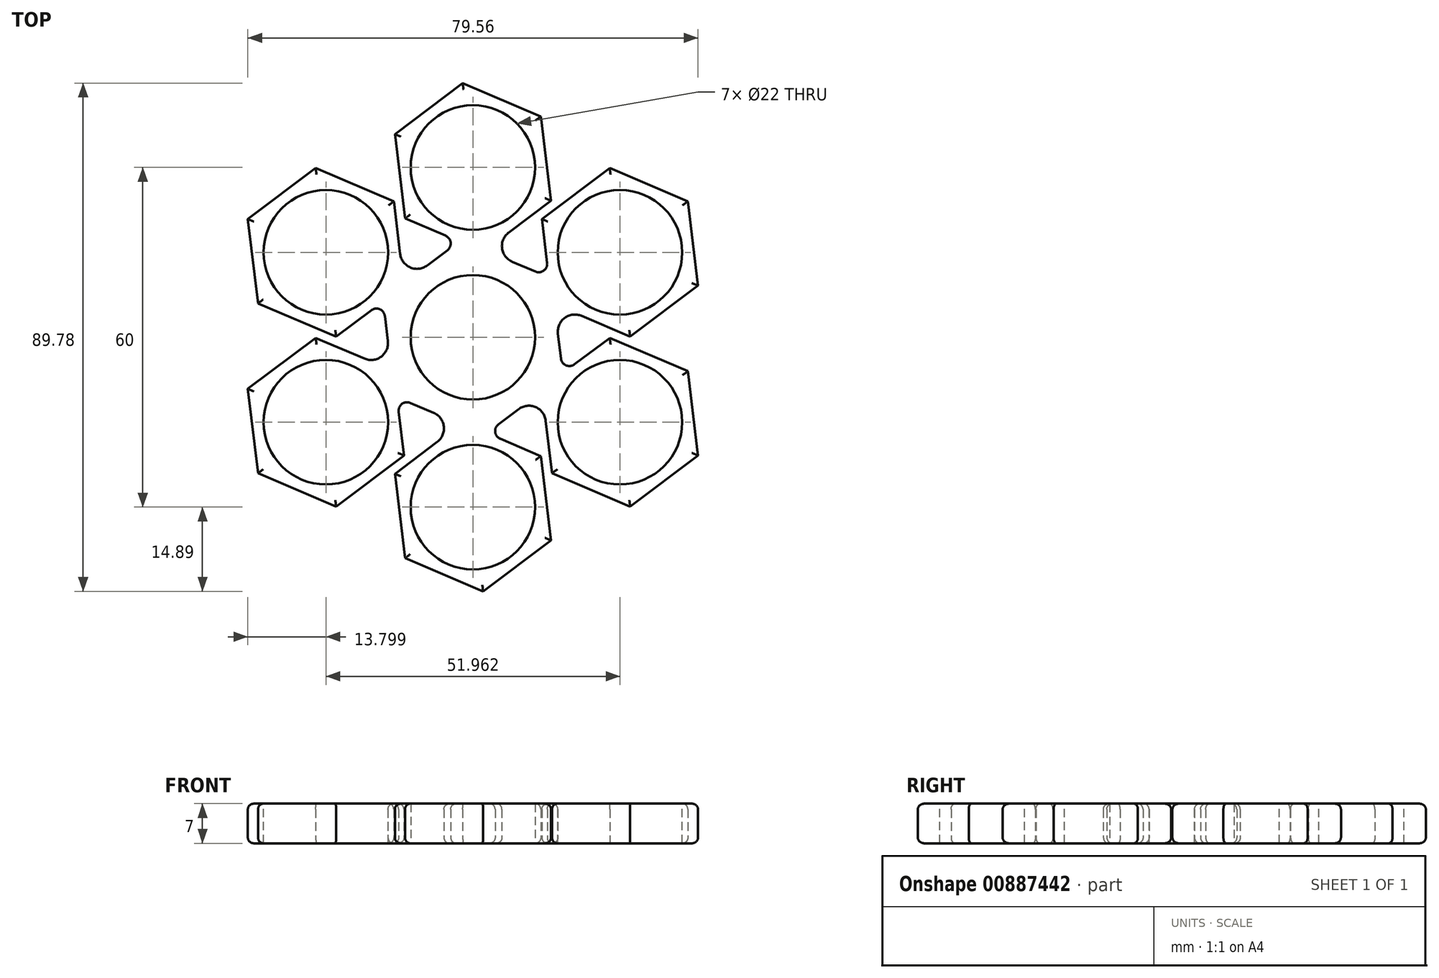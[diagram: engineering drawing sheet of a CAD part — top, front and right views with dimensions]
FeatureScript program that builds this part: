
annotation { "Feature Type Name" : "Feature", "Feature Type Description" : "" }
export const myFeature = defineFeature(function(context is Context, id is Id, definition is map)
    precondition{}
    {
        {
            var Q0;
            Q0=qCreatedBy(makeId("Top.planeOp"),FACE);
            var sketch = newSketch(context, id + "F0", { "sketchPlane" : qUnion([Q0])});
            skCircle(sketch, "E0", {"center": v(0, 0) * mm, "radius": 11 * mm});
            skCircle(sketch, "E1", {"center": v(0, 0) * mm, "radius": 15 * mm});
            skLineSegment(sketch, "E2", {"start": v(0, 0) * mm, "end": v(0, 30) * mm, "construction": true});
            skCircle(sketch, "E3", {"center": v(0, 30) * mm, "radius": 15 * mm, "construction": true});
            skLineSegment(sketch, "E4.2", {"start": v(-13.8, 35.88) * mm, "end": v(-1.8, 44.9) * mm});
            skLineSegment(sketch, "E4.3", {"start": v(-1.8, 44.9) * mm, "end": v(12, 39) * mm});
            skLineSegment(sketch, "E4.4", {"start": v(12, 39) * mm, "end": v(13.8, 24.12) * mm});
            skLineSegment(sketch, "E4.5", {"start": v(13.8, 24.12) * mm, "end": v(1.55, 14.92) * mm});
            skLineSegment(sketch, "E5.0", {"start": v(9.55, 25.93) * mm, "end": v(-9, 12) * mm});
            skLineSegment(sketch, "E5.1", {"start": v(8.3, 36.23) * mm, "end": v(9.55, 25.93) * mm});
            skLineSegment(sketch, "E5.2", {"start": v(-1.25, 40.3) * mm, "end": v(8.3, 36.23) * mm});
            skLineSegment(sketch, "E5.3", {"start": v(-11.4, 32.69) * mm, "end": v(-1.25, 40.3) * mm});
            skLineSegment(sketch, "E6", {"start": v(-11.4, 32.69) * mm, "end": v(-13.8, 35.88) * mm, "construction": true});
            skLineSegment(sketch, "E7", {"start": v(-12.6, 34.29) * mm, "end": v(-13.52, 33.6) * mm, "construction": true});
            skLineSegment(sketch, "E8", {"start": v(-13.52, 33.6) * mm, "end": v(-13.8, 35.88) * mm});
            skLineSegment(sketch, "E9", {"start": v(-11.4, 32.69) * mm, "end": v(-13.52, 33.6) * mm});
            skLineSegment(sketch, "E10.1.0", {"start": v(-37.98, 6) * mm, "end": v(-39.78, 20.88) * mm});
            skLineSegment(sketch, "E10.1.1", {"start": v(-39.78, 20.88) * mm, "end": v(-27.78, 29.9) * mm});
            skLineSegment(sketch, "E10.1.2", {"start": v(-34, 6.47) * mm, "end": v(-35.53, 19.07) * mm});
            skLineSegment(sketch, "E10.1.3", {"start": v(-35.53, 19.07) * mm, "end": v(-27.23, 25.3) * mm});
            skLineSegment(sketch, "E10.1.4", {"start": v(-35.85, 5.09) * mm, "end": v(-37.98, 6) * mm});
            skLineSegment(sketch, "E10.1.5", {"start": v(-34, 6.47) * mm, "end": v(-35.85, 5.09) * mm});
            skLineSegment(sketch, "E10.1.6", {"start": v(-27.78, 29.9) * mm, "end": v(-13.99, 24) * mm});
            skLineSegment(sketch, "E10.1.7", {"start": v(-27.23, 25.3) * mm, "end": v(-17.68, 21.23) * mm});
            skLineSegment(sketch, "E10.1.8", {"start": v(-13.99, 24) * mm, "end": v(-12.15, 8.8) * mm});
            skLineSegment(sketch, "E10.1.9", {"start": v(-17.68, 21.23) * mm, "end": v(-14.9, -1.8) * mm});
            skLineSegment(sketch, "E10.2.0", {"start": v(-24.18, -29.9) * mm, "end": v(-37.98, -24) * mm});
            skLineSegment(sketch, "E10.2.1", {"start": v(-37.98, -24) * mm, "end": v(-39.78, -9.12) * mm});
            skLineSegment(sketch, "E10.2.2", {"start": v(-22.6, -26.21) * mm, "end": v(-34.28, -21.23) * mm});
            skLineSegment(sketch, "E10.2.3", {"start": v(-34.28, -21.23) * mm, "end": v(-35.53, -10.93) * mm});
            skLineSegment(sketch, "E10.2.4", {"start": v(-22.33, -28.5) * mm, "end": v(-24.18, -29.9) * mm});
            skLineSegment(sketch, "E10.2.5", {"start": v(-22.6, -26.21) * mm, "end": v(-22.33, -28.5) * mm});
            skLineSegment(sketch, "E10.2.6", {"start": v(-39.78, -9.12) * mm, "end": v(-27.78, -0.1) * mm});
            skLineSegment(sketch, "E10.2.7", {"start": v(-35.53, -10.93) * mm, "end": v(-27.23, -4.7) * mm});
            skLineSegment(sketch, "E10.2.8", {"start": v(-27.78, -0.1) * mm, "end": v(-13.7, -6.12) * mm});
            skLineSegment(sketch, "E10.2.9", {"start": v(-27.23, -4.7) * mm, "end": v(-5.88, -13.8) * mm});
            skLineSegment(sketch, "E10.3.0", {"start": v(13.8, -35.88) * mm, "end": v(1.8, -44.9) * mm});
            skLineSegment(sketch, "E10.3.1", {"start": v(1.8, -44.9) * mm, "end": v(-12, -39) * mm});
            skLineSegment(sketch, "E10.3.2", {"start": v(11.4, -32.69) * mm, "end": v(1.25, -40.3) * mm});
            skLineSegment(sketch, "E10.3.3", {"start": v(1.25, -40.3) * mm, "end": v(-8.3, -36.23) * mm});
            skLineSegment(sketch, "E10.3.4", {"start": v(13.52, -33.6) * mm, "end": v(13.8, -35.88) * mm});
            skLineSegment(sketch, "E10.3.5", {"start": v(11.4, -32.69) * mm, "end": v(13.52, -33.6) * mm});
            skLineSegment(sketch, "E10.3.6", {"start": v(-12, -39) * mm, "end": v(-13.8, -24.12) * mm});
            skLineSegment(sketch, "E10.3.7", {"start": v(-8.3, -36.23) * mm, "end": v(-9.55, -25.93) * mm});
            skLineSegment(sketch, "E10.3.8", {"start": v(-13.8, -24.12) * mm, "end": v(-1.55, -14.92) * mm});
            skLineSegment(sketch, "E10.3.9", {"start": v(-9.55, -25.93) * mm, "end": v(9, -12) * mm});
            skLineSegment(sketch, "E10.4.0", {"start": v(37.98, -6) * mm, "end": v(39.78, -20.88) * mm});
            skLineSegment(sketch, "E10.4.1", {"start": v(39.78, -20.88) * mm, "end": v(27.78, -29.9) * mm});
            skLineSegment(sketch, "E10.4.2", {"start": v(34, -6.47) * mm, "end": v(35.53, -19.07) * mm});
            skLineSegment(sketch, "E10.4.3", {"start": v(35.53, -19.07) * mm, "end": v(27.23, -25.3) * mm});
            skLineSegment(sketch, "E10.4.4", {"start": v(35.85, -5.09) * mm, "end": v(37.98, -6) * mm});
            skLineSegment(sketch, "E10.4.5", {"start": v(34, -6.47) * mm, "end": v(35.85, -5.09) * mm});
            skLineSegment(sketch, "E10.4.6", {"start": v(27.78, -29.9) * mm, "end": v(13.99, -24) * mm});
            skLineSegment(sketch, "E10.4.7", {"start": v(27.23, -25.3) * mm, "end": v(17.68, -21.23) * mm});
            skLineSegment(sketch, "E10.4.8", {"start": v(13.99, -24) * mm, "end": v(12.15, -8.8) * mm});
            skLineSegment(sketch, "E10.4.9", {"start": v(17.68, -21.23) * mm, "end": v(14.9, 1.8) * mm});
            skLineSegment(sketch, "E10.5.0", {"start": v(24.18, 29.9) * mm, "end": v(37.98, 24) * mm});
            skLineSegment(sketch, "E10.5.1", {"start": v(37.98, 24) * mm, "end": v(39.78, 9.12) * mm});
            skLineSegment(sketch, "E10.5.2", {"start": v(22.6, 26.21) * mm, "end": v(34.28, 21.23) * mm});
            skLineSegment(sketch, "E10.5.3", {"start": v(34.28, 21.23) * mm, "end": v(35.53, 10.93) * mm});
            skLineSegment(sketch, "E10.5.4", {"start": v(22.33, 28.5) * mm, "end": v(24.18, 29.9) * mm});
            skLineSegment(sketch, "E10.5.5", {"start": v(22.6, 26.21) * mm, "end": v(22.33, 28.5) * mm});
            skLineSegment(sketch, "E10.5.6", {"start": v(39.78, 9.12) * mm, "end": v(27.78, 0.1) * mm});
            skLineSegment(sketch, "E10.5.7", {"start": v(35.53, 10.93) * mm, "end": v(27.23, 4.7) * mm});
            skLineSegment(sketch, "E10.5.8", {"start": v(27.78, 0.1) * mm, "end": v(13.7, 6.12) * mm});
            skLineSegment(sketch, "E10.5.9", {"start": v(27.23, 4.7) * mm, "end": v(5.88, 13.8) * mm});
            skLineSegment(sketch, "E11.1", {"start": v(13.8, 24.12) * mm, "end": v(1.8, 15.1) * mm});
            skLineSegment(sketch, "E11.2", {"start": v(1.8, 15.1) * mm, "end": v(-12, 21) * mm});
            skLineSegment(sketch, "E11.3", {"start": v(-12, 21) * mm, "end": v(-13.8, 35.88) * mm});
            skLineSegment(sketch, "E12.1.0", {"start": v(-24.18, 0.1) * mm, "end": v(-37.98, 6) * mm});
            skLineSegment(sketch, "E12.1.1", {"start": v(-12.18, 9.12) * mm, "end": v(-24.18, 0.1) * mm});
            skLineSegment(sketch, "E12.2.0", {"start": v(-12.18, -20.88) * mm, "end": v(-24.18, -29.9) * mm});
            skLineSegment(sketch, "E12.2.1", {"start": v(-13.99, -6) * mm, "end": v(-12.18, -20.88) * mm});
            skLineSegment(sketch, "E12.3.0", {"start": v(12, -21) * mm, "end": v(13.8, -35.88) * mm});
            skLineSegment(sketch, "E12.3.1", {"start": v(-1.8, -15.1) * mm, "end": v(12, -21) * mm});
            skLineSegment(sketch, "E12.4.0", {"start": v(24.18, -0.1) * mm, "end": v(37.98, -6) * mm});
            skLineSegment(sketch, "E12.4.1", {"start": v(12.18, -9.12) * mm, "end": v(24.18, -0.1) * mm});
            skLineSegment(sketch, "E12.5.0", {"start": v(12.18, 20.88) * mm, "end": v(24.18, 29.9) * mm});
            skLineSegment(sketch, "E12.5.1", {"start": v(13.99, 6) * mm, "end": v(12.18, 20.88) * mm});
            skSolve(sketch);
        }
        {
            var Q0;
            Q0 = qSketchRegion(id + "F0", true);
            extrude(context, id + "F1", {"entities" : qUnion([Q0]), "depth" : 7 * mm, "offsetDistance" : 25 * mm});
        }
        {
            var Q0;
            Q0=makeQuery(id+"F1.opExtrude","SWEPT_EDGE",EDGE,{"disambiguationData":[OSD([sQuery(id+"F0.wireOp",EDGE,"E5.0"),sQuery(id+"F0.wireOp",EDGE,"E11.2")])]});
            var Q1;
            Q1=makeQuery(id+"F1.opExtrude","SWEPT_EDGE",EDGE,{"disambiguationData":[OSD([sQuery(id+"F0.wireOp",EDGE,"E10.5.9"),sQuery(id+"F0.wireOp",EDGE,"E12.5.1")])]});
            var Q2;
            Q2=makeQuery(id+"F1.opExtrude","SWEPT_EDGE",EDGE,{"disambiguationData":[OSD([sQuery(id+"F0.wireOp",EDGE,"E10.4.9"),sQuery(id+"F0.wireOp",EDGE,"E12.4.1")])]});
            var Q3;
            Q3=makeQuery(id+"F1.opExtrude","SWEPT_EDGE",EDGE,{"disambiguationData":[OSD([sQuery(id+"F0.wireOp",EDGE,"E10.3.9"),sQuery(id+"F0.wireOp",EDGE,"E12.3.1")])]});
            var Q4;
            Q4=makeQuery(id+"F1.opExtrude","SWEPT_EDGE",EDGE,{"disambiguationData":[OSD([sQuery(id+"F0.wireOp",EDGE,"E10.2.9"),sQuery(id+"F0.wireOp",EDGE,"E12.2.1")])]});
            var Q5;
            Q5=makeQuery(id+"F1.opExtrude","SWEPT_EDGE",EDGE,{"disambiguationData":[OSD([sQuery(id+"F0.wireOp",EDGE,"E10.1.9"),sQuery(id+"F0.wireOp",EDGE,"E12.1.1")])]});
            fillet(context, id + "F2", {"entities" : qUnion([Q0, Q1, Q2, Q3, Q4, Q5]), "radius" : 1.5 * mm, "tangentPropagation" : true, "allowEdgeOverflow" : false});
        }
        {
            var Q0;
            Q0=makeQuery(id+"F1.opExtrude","SWEPT_EDGE",EDGE,{"disambiguationData":[OSD([sQuery(id+"F0.wireOp",EDGE,"E1"),sQuery(id+"F0.wireOp",EDGE,"E10.3.8")])]});
            var Q1;
            Q1=makeQuery(id+"F1.opExtrude","SWEPT_EDGE",EDGE,{"disambiguationData":[OSD([sQuery(id+"F0.wireOp",EDGE,"E1"),sQuery(id+"F0.wireOp",EDGE,"E10.2.8")])]});
            var Q2;
            Q2=makeQuery(id+"F1.opExtrude","SWEPT_EDGE",EDGE,{"disambiguationData":[OSD([sQuery(id+"F0.wireOp",EDGE,"E1"),sQuery(id+"F0.wireOp",EDGE,"E10.1.8")])]});
            var Q3;
            Q3=makeQuery(id+"F1.opExtrude","SWEPT_EDGE",EDGE,{"disambiguationData":[OSD([sQuery(id+"F0.wireOp",EDGE,"E1"),sQuery(id+"F0.wireOp",EDGE,"E4.5")])]});
            var Q4;
            Q4=makeQuery(id+"F1.opExtrude","SWEPT_EDGE",EDGE,{"disambiguationData":[OSD([sQuery(id+"F0.wireOp",EDGE,"E1"),sQuery(id+"F0.wireOp",EDGE,"E10.5.8")])]});
            var Q5;
            Q5=makeQuery(id+"F1.opExtrude","SWEPT_EDGE",EDGE,{"disambiguationData":[OSD([sQuery(id+"F0.wireOp",EDGE,"E1"),sQuery(id+"F0.wireOp",EDGE,"E10.4.8")])]});
            fillet(context, id + "F3", {"entities" : qUnion([Q0, Q1, Q2, Q3, Q4, Q5]), "radius" : 3 * mm, "tangentPropagation" : true, "allowEdgeOverflow" : false});
        }
        {
            var Q0;
            Q0=makeQuery(id+"F1.opExtrude","CAP_FACE",FACE,{"disambiguationData":[OSD([sQuery(id+"F0.wireOp",EDGE,"E0"),sQuery(id+"F0.wireOp",EDGE,"E1"),sQuery(id+"F0.wireOp",EDGE,"E4.2"),sQuery(id+"F0.wireOp",EDGE,"E4.3"),sQuery(id+"F0.wireOp",EDGE,"E4.4"),sQuery(id+"F0.wireOp",EDGE,"E4.5"),sQuery(id+"F0.wireOp",EDGE,"E5.0"),sQuery(id+"F0.wireOp",EDGE,"E5.1"),sQuery(id+"F0.wireOp",EDGE,"E5.2"),sQuery(id+"F0.wireOp",EDGE,"E5.3"),sQuery(id+"F0.wireOp",EDGE,"E8"),sQuery(id+"F0.wireOp",EDGE,"E9"),sQuery(id+"F0.wireOp",EDGE,"E10.1.0"),sQuery(id+"F0.wireOp",EDGE,"E10.1.1"),sQuery(id+"F0.wireOp",EDGE,"E10.1.2"),sQuery(id+"F0.wireOp",EDGE,"E10.1.3"),sQuery(id+"F0.wireOp",EDGE,"E10.1.4"),sQuery(id+"F0.wireOp",EDGE,"E10.1.5"),sQuery(id+"F0.wireOp",EDGE,"E10.1.6"),sQuery(id+"F0.wireOp",EDGE,"E10.1.7"),sQuery(id+"F0.wireOp",EDGE,"E10.1.8"),sQuery(id+"F0.wireOp",EDGE,"E10.1.9"),sQuery(id+"F0.wireOp",EDGE,"E10.2.0"),sQuery(id+"F0.wireOp",EDGE,"E10.2.1"),sQuery(id+"F0.wireOp",EDGE,"E10.2.2"),sQuery(id+"F0.wireOp",EDGE,"E10.2.3"),sQuery(id+"F0.wireOp",EDGE,"E10.2.4"),sQuery(id+"F0.wireOp",EDGE,"E10.2.5"),sQuery(id+"F0.wireOp",EDGE,"E10.2.6"),sQuery(id+"F0.wireOp",EDGE,"E10.2.7"),sQuery(id+"F0.wireOp",EDGE,"E10.2.8"),sQuery(id+"F0.wireOp",EDGE,"E10.2.9"),sQuery(id+"F0.wireOp",EDGE,"E10.3.0"),sQuery(id+"F0.wireOp",EDGE,"E10.3.1"),sQuery(id+"F0.wireOp",EDGE,"E10.3.2"),sQuery(id+"F0.wireOp",EDGE,"E10.3.3"),sQuery(id+"F0.wireOp",EDGE,"E10.3.4"),sQuery(id+"F0.wireOp",EDGE,"E10.3.5"),sQuery(id+"F0.wireOp",EDGE,"E10.3.6"),sQuery(id+"F0.wireOp",EDGE,"E10.3.7"),sQuery(id+"F0.wireOp",EDGE,"E10.3.8"),sQuery(id+"F0.wireOp",EDGE,"E10.3.9"),sQuery(id+"F0.wireOp",EDGE,"E10.4.0"),sQuery(id+"F0.wireOp",EDGE,"E10.4.1"),sQuery(id+"F0.wireOp",EDGE,"E10.4.2"),sQuery(id+"F0.wireOp",EDGE,"E10.4.3"),sQuery(id+"F0.wireOp",EDGE,"E10.4.4"),sQuery(id+"F0.wireOp",EDGE,"E10.4.5"),sQuery(id+"F0.wireOp",EDGE,"E10.4.6"),sQuery(id+"F0.wireOp",EDGE,"E10.4.7"),sQuery(id+"F0.wireOp",EDGE,"E10.4.8"),sQuery(id+"F0.wireOp",EDGE,"E10.4.9"),sQuery(id+"F0.wireOp",EDGE,"E10.5.0"),sQuery(id+"F0.wireOp",EDGE,"E10.5.1"),sQuery(id+"F0.wireOp",EDGE,"E10.5.2"),sQuery(id+"F0.wireOp",EDGE,"E10.5.3"),sQuery(id+"F0.wireOp",EDGE,"E10.5.4"),sQuery(id+"F0.wireOp",EDGE,"E10.5.5"),sQuery(id+"F0.wireOp",EDGE,"E10.5.6"),sQuery(id+"F0.wireOp",EDGE,"E10.5.7"),sQuery(id+"F0.wireOp",EDGE,"E10.5.8"),sQuery(id+"F0.wireOp",EDGE,"E10.5.9")])],"isStart":true});
            var Q1;
            Q1=makeQuery(id+"F1.opExtrude","CAP_FACE",FACE,{"disambiguationData":[OSD([sQuery(id+"F0.wireOp",EDGE,"E0"),sQuery(id+"F0.wireOp",EDGE,"E1"),sQuery(id+"F0.wireOp",EDGE,"E4.2"),sQuery(id+"F0.wireOp",EDGE,"E4.3"),sQuery(id+"F0.wireOp",EDGE,"E4.4"),sQuery(id+"F0.wireOp",EDGE,"E4.5"),sQuery(id+"F0.wireOp",EDGE,"E5.0"),sQuery(id+"F0.wireOp",EDGE,"E5.1"),sQuery(id+"F0.wireOp",EDGE,"E5.2"),sQuery(id+"F0.wireOp",EDGE,"E5.3"),sQuery(id+"F0.wireOp",EDGE,"E8"),sQuery(id+"F0.wireOp",EDGE,"E9"),sQuery(id+"F0.wireOp",EDGE,"E10.1.0"),sQuery(id+"F0.wireOp",EDGE,"E10.1.1"),sQuery(id+"F0.wireOp",EDGE,"E10.1.2"),sQuery(id+"F0.wireOp",EDGE,"E10.1.3"),sQuery(id+"F0.wireOp",EDGE,"E10.1.4"),sQuery(id+"F0.wireOp",EDGE,"E10.1.5"),sQuery(id+"F0.wireOp",EDGE,"E10.1.6"),sQuery(id+"F0.wireOp",EDGE,"E10.1.7"),sQuery(id+"F0.wireOp",EDGE,"E10.1.8"),sQuery(id+"F0.wireOp",EDGE,"E10.1.9"),sQuery(id+"F0.wireOp",EDGE,"E10.2.0"),sQuery(id+"F0.wireOp",EDGE,"E10.2.1"),sQuery(id+"F0.wireOp",EDGE,"E10.2.2"),sQuery(id+"F0.wireOp",EDGE,"E10.2.3"),sQuery(id+"F0.wireOp",EDGE,"E10.2.4"),sQuery(id+"F0.wireOp",EDGE,"E10.2.5"),sQuery(id+"F0.wireOp",EDGE,"E10.2.6"),sQuery(id+"F0.wireOp",EDGE,"E10.2.7"),sQuery(id+"F0.wireOp",EDGE,"E10.2.8"),sQuery(id+"F0.wireOp",EDGE,"E10.2.9"),sQuery(id+"F0.wireOp",EDGE,"E10.3.0"),sQuery(id+"F0.wireOp",EDGE,"E10.3.1"),sQuery(id+"F0.wireOp",EDGE,"E10.3.2"),sQuery(id+"F0.wireOp",EDGE,"E10.3.3"),sQuery(id+"F0.wireOp",EDGE,"E10.3.4"),sQuery(id+"F0.wireOp",EDGE,"E10.3.5"),sQuery(id+"F0.wireOp",EDGE,"E10.3.6"),sQuery(id+"F0.wireOp",EDGE,"E10.3.7"),sQuery(id+"F0.wireOp",EDGE,"E10.3.8"),sQuery(id+"F0.wireOp",EDGE,"E10.3.9"),sQuery(id+"F0.wireOp",EDGE,"E10.4.0"),sQuery(id+"F0.wireOp",EDGE,"E10.4.1"),sQuery(id+"F0.wireOp",EDGE,"E10.4.2"),sQuery(id+"F0.wireOp",EDGE,"E10.4.3"),sQuery(id+"F0.wireOp",EDGE,"E10.4.4"),sQuery(id+"F0.wireOp",EDGE,"E10.4.5"),sQuery(id+"F0.wireOp",EDGE,"E10.4.6"),sQuery(id+"F0.wireOp",EDGE,"E10.4.7"),sQuery(id+"F0.wireOp",EDGE,"E10.4.8"),sQuery(id+"F0.wireOp",EDGE,"E10.4.9"),sQuery(id+"F0.wireOp",EDGE,"E10.5.0"),sQuery(id+"F0.wireOp",EDGE,"E10.5.1"),sQuery(id+"F0.wireOp",EDGE,"E10.5.2"),sQuery(id+"F0.wireOp",EDGE,"E10.5.3"),sQuery(id+"F0.wireOp",EDGE,"E10.5.4"),sQuery(id+"F0.wireOp",EDGE,"E10.5.5"),sQuery(id+"F0.wireOp",EDGE,"E10.5.6"),sQuery(id+"F0.wireOp",EDGE,"E10.5.7"),sQuery(id+"F0.wireOp",EDGE,"E10.5.8"),sQuery(id+"F0.wireOp",EDGE,"E10.5.9")])],"isStart":false});
            fillet(context, id + "F4", {"entities" : qUnion([Q0, Q1]), "radius" : 1 * mm, "tangentPropagation" : true, "allowEdgeOverflow" : false});
        }
        {
            var Q0;
            Q0=qCreatedBy(makeId("Top.planeOp"),FACE);
            var sketch = newSketch(context, id + "F5", { "sketchPlane" : qUnion([Q0])});
            skCircle(sketch, "E13", {"center": v(0, 0) * mm, "radius": 11 * mm});
            skCircle(sketch, "E14", {"center": v(0, 0) * mm, "radius": 13.02 * mm});
            skSolve(sketch);
        }
        {
            var Q0;
            Q0=makeQuery(id+"F5.imprint","IMPRINT",FACE,{"disambiguationData":[TD([[makeQuery(id+"F5.imprint","IMPRINT",EDGE,{"derivedFrom":sQuery(id+"F5.wireOp",EDGE,"E13")}),-1.0]])]});
            var Q1;
            Q1=makeQuery(id+"F1.opExtrude","CAP_FACE",FACE,{"disambiguationData":[OSD([sQuery(id+"F0.wireOp",EDGE,"E0"),sQuery(id+"F0.wireOp",EDGE,"E1"),sQuery(id+"F0.wireOp",EDGE,"E4.2"),sQuery(id+"F0.wireOp",EDGE,"E4.3"),sQuery(id+"F0.wireOp",EDGE,"E4.4"),sQuery(id+"F0.wireOp",EDGE,"E4.5"),sQuery(id+"F0.wireOp",EDGE,"E5.0"),sQuery(id+"F0.wireOp",EDGE,"E5.1"),sQuery(id+"F0.wireOp",EDGE,"E5.2"),sQuery(id+"F0.wireOp",EDGE,"E5.3"),sQuery(id+"F0.wireOp",EDGE,"E8"),sQuery(id+"F0.wireOp",EDGE,"E9"),sQuery(id+"F0.wireOp",EDGE,"E10.1.0"),sQuery(id+"F0.wireOp",EDGE,"E10.1.1"),sQuery(id+"F0.wireOp",EDGE,"E10.1.2"),sQuery(id+"F0.wireOp",EDGE,"E10.1.3"),sQuery(id+"F0.wireOp",EDGE,"E10.1.4"),sQuery(id+"F0.wireOp",EDGE,"E10.1.5"),sQuery(id+"F0.wireOp",EDGE,"E10.1.6"),sQuery(id+"F0.wireOp",EDGE,"E10.1.7"),sQuery(id+"F0.wireOp",EDGE,"E10.1.8"),sQuery(id+"F0.wireOp",EDGE,"E10.1.9"),sQuery(id+"F0.wireOp",EDGE,"E10.2.0"),sQuery(id+"F0.wireOp",EDGE,"E10.2.1"),sQuery(id+"F0.wireOp",EDGE,"E10.2.2"),sQuery(id+"F0.wireOp",EDGE,"E10.2.3"),sQuery(id+"F0.wireOp",EDGE,"E10.2.4"),sQuery(id+"F0.wireOp",EDGE,"E10.2.5"),sQuery(id+"F0.wireOp",EDGE,"E10.2.6"),sQuery(id+"F0.wireOp",EDGE,"E10.2.7"),sQuery(id+"F0.wireOp",EDGE,"E10.2.8"),sQuery(id+"F0.wireOp",EDGE,"E10.2.9"),sQuery(id+"F0.wireOp",EDGE,"E10.3.0"),sQuery(id+"F0.wireOp",EDGE,"E10.3.1"),sQuery(id+"F0.wireOp",EDGE,"E10.3.2"),sQuery(id+"F0.wireOp",EDGE,"E10.3.3"),sQuery(id+"F0.wireOp",EDGE,"E10.3.4"),sQuery(id+"F0.wireOp",EDGE,"E10.3.5"),sQuery(id+"F0.wireOp",EDGE,"E10.3.6"),sQuery(id+"F0.wireOp",EDGE,"E10.3.7"),sQuery(id+"F0.wireOp",EDGE,"E10.3.8"),sQuery(id+"F0.wireOp",EDGE,"E10.3.9"),sQuery(id+"F0.wireOp",EDGE,"E10.4.0"),sQuery(id+"F0.wireOp",EDGE,"E10.4.1"),sQuery(id+"F0.wireOp",EDGE,"E10.4.2"),sQuery(id+"F0.wireOp",EDGE,"E10.4.3"),sQuery(id+"F0.wireOp",EDGE,"E10.4.4"),sQuery(id+"F0.wireOp",EDGE,"E10.4.5"),sQuery(id+"F0.wireOp",EDGE,"E10.4.6"),sQuery(id+"F0.wireOp",EDGE,"E10.4.7"),sQuery(id+"F0.wireOp",EDGE,"E10.4.8"),sQuery(id+"F0.wireOp",EDGE,"E10.4.9"),sQuery(id+"F0.wireOp",EDGE,"E10.5.0"),sQuery(id+"F0.wireOp",EDGE,"E10.5.1"),sQuery(id+"F0.wireOp",EDGE,"E10.5.2"),sQuery(id+"F0.wireOp",EDGE,"E10.5.3"),sQuery(id+"F0.wireOp",EDGE,"E10.5.4"),sQuery(id+"F0.wireOp",EDGE,"E10.5.5"),sQuery(id+"F0.wireOp",EDGE,"E10.5.6"),sQuery(id+"F0.wireOp",EDGE,"E10.5.7"),sQuery(id+"F0.wireOp",EDGE,"E10.5.8"),sQuery(id+"F0.wireOp",EDGE,"E10.5.9")])],"isStart":false});
            extrude(context, id + "F6", {"entities" : qUnion([Q0]), "operationType" : NewBodyOperationType.ADD, "endBound" : BoundingType.UP_TO_SURFACE, "depth" : 25 * mm, "endBoundEntityFace" : qUnion([Q1]), "offsetDistance" : 25 * mm});
        }
        {
            var Q0;
            Q0=makeQuery(id+"F6.boolean.opBoolean","MERGE",FACE,{"derivedFrom":[makeQuery(id+"F1.opExtrude","CAP_FACE",FACE,{"disambiguationData":[OSD([sQuery(id+"F0.wireOp",EDGE,"E0"),sQuery(id+"F0.wireOp",EDGE,"E1"),sQuery(id+"F0.wireOp",EDGE,"E4.5"),sQuery(id+"F0.wireOp",EDGE,"E5.0"),sQuery(id+"F0.wireOp",EDGE,"E10.1.0"),sQuery(id+"F0.wireOp",EDGE,"E10.1.1"),sQuery(id+"F0.wireOp",EDGE,"E10.1.6"),sQuery(id+"F0.wireOp",EDGE,"E10.1.8"),sQuery(id+"F0.wireOp",EDGE,"E10.1.9"),sQuery(id+"F0.wireOp",EDGE,"E10.2.0"),sQuery(id+"F0.wireOp",EDGE,"E10.2.1"),sQuery(id+"F0.wireOp",EDGE,"E10.2.6"),sQuery(id+"F0.wireOp",EDGE,"E10.2.8"),sQuery(id+"F0.wireOp",EDGE,"E10.2.9"),sQuery(id+"F0.wireOp",EDGE,"E10.3.0"),sQuery(id+"F0.wireOp",EDGE,"E10.3.1"),sQuery(id+"F0.wireOp",EDGE,"E10.3.6"),sQuery(id+"F0.wireOp",EDGE,"E10.3.8"),sQuery(id+"F0.wireOp",EDGE,"E10.3.9"),sQuery(id+"F0.wireOp",EDGE,"E10.4.0"),sQuery(id+"F0.wireOp",EDGE,"E10.4.1"),sQuery(id+"F0.wireOp",EDGE,"E10.4.6"),sQuery(id+"F0.wireOp",EDGE,"E10.4.8"),sQuery(id+"F0.wireOp",EDGE,"E10.4.9"),sQuery(id+"F0.wireOp",EDGE,"E10.5.0"),sQuery(id+"F0.wireOp",EDGE,"E10.5.1"),sQuery(id+"F0.wireOp",EDGE,"E10.5.6"),sQuery(id+"F0.wireOp",EDGE,"E10.5.8"),sQuery(id+"F0.wireOp",EDGE,"E10.5.9"),sQuery(id+"F0.wireOp",EDGE,"E4.4"),sQuery(id+"F0.wireOp",EDGE,"E11.1"),sQuery(id+"F0.wireOp",EDGE,"E11.2"),sQuery(id+"F0.wireOp",EDGE,"E11.3"),sQuery(id+"F0.wireOp",EDGE,"E4.2"),sQuery(id+"F0.wireOp",EDGE,"E4.3"),sQuery(id+"F0.wireOp",EDGE,"E12.1.0"),sQuery(id+"F0.wireOp",EDGE,"E12.1.1"),sQuery(id+"F0.wireOp",EDGE,"E12.2.0"),sQuery(id+"F0.wireOp",EDGE,"E12.2.1"),sQuery(id+"F0.wireOp",EDGE,"E12.3.0"),sQuery(id+"F0.wireOp",EDGE,"E12.3.1"),sQuery(id+"F0.wireOp",EDGE,"E12.4.0"),sQuery(id+"F0.wireOp",EDGE,"E12.4.1"),sQuery(id+"F0.wireOp",EDGE,"E12.5.0"),sQuery(id+"F0.wireOp",EDGE,"E12.5.1")])],"isStart":false}),makeQuery(id+"F6.opExtrude","CAP_FACE",FACE,{"disambiguationData":[OSD([sQuery(id+"F5.wireOp",EDGE,"E13"),sQuery(id+"F5.wireOp",EDGE,"E14")])],"isStart":false})]});
            var sketch = newSketch(context, id + "F7", { "sketchPlane" : qUnion([Q0])});
            skCircle(sketch, "E15", {"center": v(0, 0) * mm, "radius": 30 * mm});
            skPoint(sketch, "E16", {"position": v(0, 30) * mm});
            skPoint(sketch, "E17.1.0", {"position": v(-25.98, 15) * mm});
            skPoint(sketch, "E17.2.0", {"position": v(-25.98, -15) * mm});
            skPoint(sketch, "E17.3.0", {"position": v(0, -30) * mm});
            skCircle(sketch, "E17.3.1", {"center": v(0, 0) * mm, "radius": 30 * mm, "construction": true});
            skPoint(sketch, "E17.4.0", {"position": v(25.98, -15) * mm});
            skPoint(sketch, "E17.5.0", {"position": v(25.98, 15) * mm});
            skSolve(sketch);
        }
        {
            var Q0;
            Q0=sQuery(id+"F7.wireOp",VERTEX,"E16");
            var Q1;
            Q1=sQuery(id+"F7.wireOp",VERTEX,"E17.1.0");
            var Q2;
            Q2=sQuery(id+"F7.wireOp",VERTEX,"E17.2.0");
            var Q3;
            Q3=sQuery(id+"F7.wireOp",VERTEX,"E17.3.0");
            var Q4;
            Q4=sQuery(id+"F7.wireOp",VERTEX,"E17.4.0");
            var Q5;
            Q5=sQuery(id+"F7.wireOp",VERTEX,"E17.5.0");
            var Q6;
            Q6=makeQuery(id+"F1.opExtrude","SWEPT_BODY",BODY,{"disambiguationData":[OSD([sQuery(id+"F0.wireOp",EDGE,"E0"),sQuery(id+"F0.wireOp",EDGE,"E1"),sQuery(id+"F0.wireOp",EDGE,"E4.5"),sQuery(id+"F0.wireOp",EDGE,"E5.0"),sQuery(id+"F0.wireOp",EDGE,"E10.1.0"),sQuery(id+"F0.wireOp",EDGE,"E10.1.1"),sQuery(id+"F0.wireOp",EDGE,"E10.1.6"),sQuery(id+"F0.wireOp",EDGE,"E10.1.8"),sQuery(id+"F0.wireOp",EDGE,"E10.1.9"),sQuery(id+"F0.wireOp",EDGE,"E10.2.0"),sQuery(id+"F0.wireOp",EDGE,"E10.2.1"),sQuery(id+"F0.wireOp",EDGE,"E10.2.6"),sQuery(id+"F0.wireOp",EDGE,"E10.2.8"),sQuery(id+"F0.wireOp",EDGE,"E10.2.9"),sQuery(id+"F0.wireOp",EDGE,"E10.3.0"),sQuery(id+"F0.wireOp",EDGE,"E10.3.1"),sQuery(id+"F0.wireOp",EDGE,"E10.3.6"),sQuery(id+"F0.wireOp",EDGE,"E10.3.8"),sQuery(id+"F0.wireOp",EDGE,"E10.3.9"),sQuery(id+"F0.wireOp",EDGE,"E10.4.0"),sQuery(id+"F0.wireOp",EDGE,"E10.4.1"),sQuery(id+"F0.wireOp",EDGE,"E10.4.6"),sQuery(id+"F0.wireOp",EDGE,"E10.4.8"),sQuery(id+"F0.wireOp",EDGE,"E10.4.9"),sQuery(id+"F0.wireOp",EDGE,"E10.5.0"),sQuery(id+"F0.wireOp",EDGE,"E10.5.1"),sQuery(id+"F0.wireOp",EDGE,"E10.5.6"),sQuery(id+"F0.wireOp",EDGE,"E10.5.8"),sQuery(id+"F0.wireOp",EDGE,"E10.5.9"),sQuery(id+"F0.wireOp",EDGE,"E4.4"),sQuery(id+"F0.wireOp",EDGE,"E11.1"),sQuery(id+"F0.wireOp",EDGE,"E11.2"),sQuery(id+"F0.wireOp",EDGE,"E11.3"),sQuery(id+"F0.wireOp",EDGE,"E4.2"),sQuery(id+"F0.wireOp",EDGE,"E4.3"),sQuery(id+"F0.wireOp",EDGE,"E12.1.0"),sQuery(id+"F0.wireOp",EDGE,"E12.1.1"),sQuery(id+"F0.wireOp",EDGE,"E12.2.0"),sQuery(id+"F0.wireOp",EDGE,"E12.2.1"),sQuery(id+"F0.wireOp",EDGE,"E12.3.0"),sQuery(id+"F0.wireOp",EDGE,"E12.3.1"),sQuery(id+"F0.wireOp",EDGE,"E12.4.0"),sQuery(id+"F0.wireOp",EDGE,"E12.4.1"),sQuery(id+"F0.wireOp",EDGE,"E12.5.0"),sQuery(id+"F0.wireOp",EDGE,"E12.5.1")])]});
            hole(context, id + "F8", {"style" : HoleStyle.SIMPLE, "endStyle" : HoleEndStyle.THROUGH, "holeDiameter" : 22 * mm, "majorDiameter" : 5 * mm, "isTappedThrough" : true, "tappedDepth" : 12 * mm, "tapClearance" : 3, "locations" : qUnion([Q0, Q1, Q2, Q3, Q4, Q5]), "scope" : qUnion([Q6])});
        }
    });
